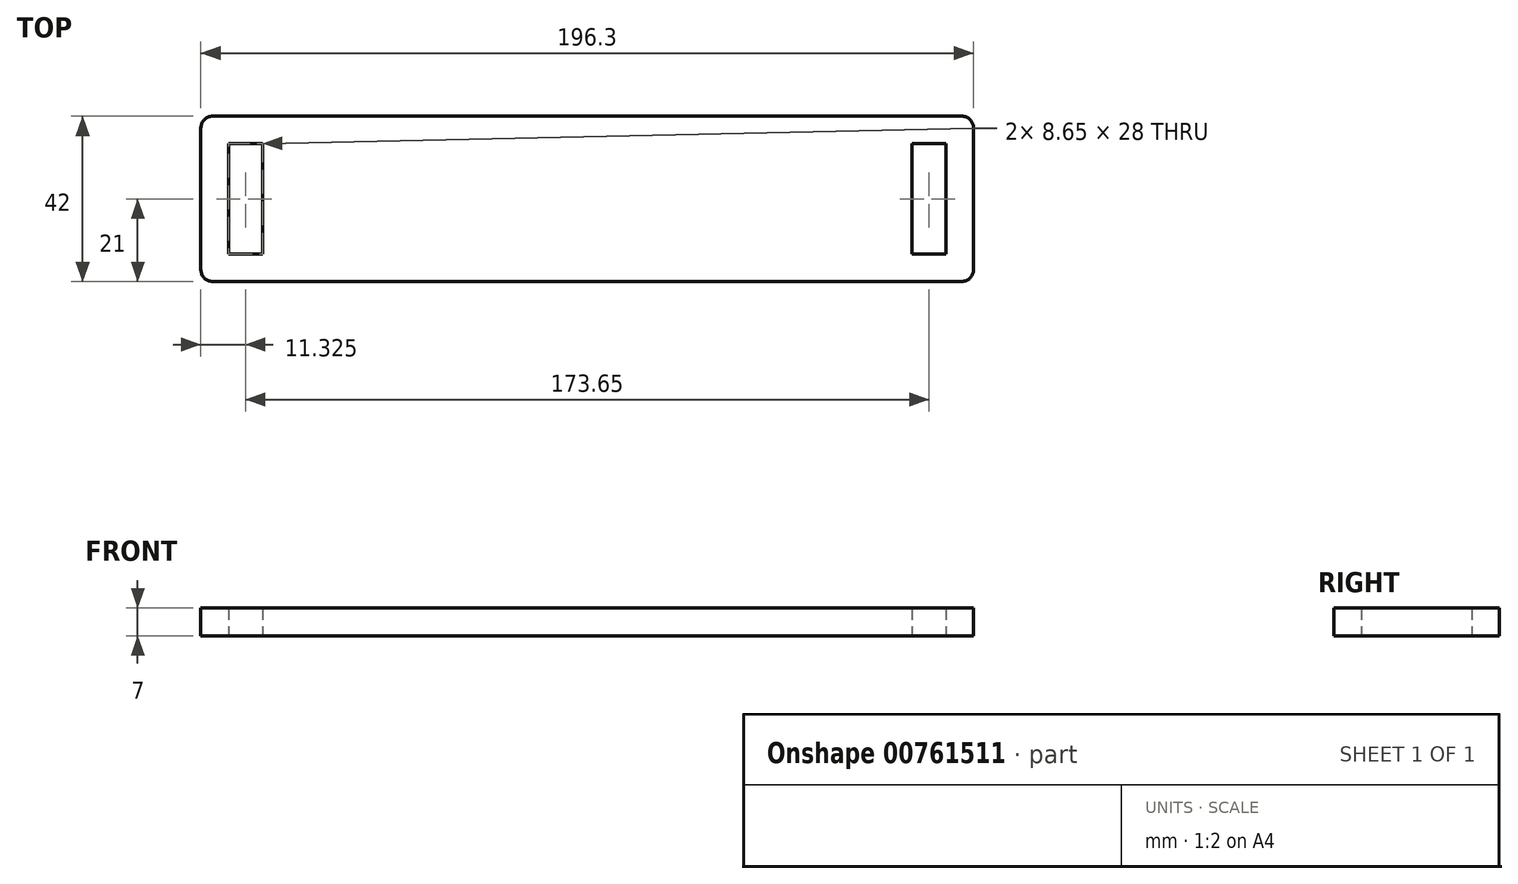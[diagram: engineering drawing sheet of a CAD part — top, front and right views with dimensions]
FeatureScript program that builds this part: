
annotation { "Feature Type Name" : "Feature", "Feature Type Description" : "" }
export const myFeature = defineFeature(function(context is Context, id is Id, definition is map)
    precondition{}
    {
        {
            var Q0;
            Q0=qCreatedBy(makeId("Top.planeOp"),FACE);
            var sketch = newSketch(context, id + "F0", { "sketchPlane" : qUnion([Q0])});
            skLineSegment(sketch, "E0.bottom", {"start": v(0, 0) * mm, "end": v(165, 0) * mm});
            skLineSegment(sketch, "E0.top", {"start": v(0, 28) * mm, "end": v(165, 28) * mm});
            skLineSegment(sketch, "E0.left", {"start": v(0, 0) * mm, "end": v(0, 28) * mm});
            skLineSegment(sketch, "E0.right", {"start": v(165, 0) * mm, "end": v(165, 28) * mm});
            skLineSegment(sketch, "E1.bottom", {"start": v(0, 28) * mm, "end": v(-8.65, 28) * mm});
            skLineSegment(sketch, "E1.top", {"start": v(0, 0) * mm, "end": v(-8.65, 0) * mm});
            skLineSegment(sketch, "E1.left", {"start": v(0, 28) * mm, "end": v(0, 0) * mm});
            skLineSegment(sketch, "E1.right", {"start": v(-8.65, 28) * mm, "end": v(-8.65, 0) * mm});
            skLineSegment(sketch, "E2.bottom", {"start": v(165, 28) * mm, "end": v(173.65, 28) * mm});
            skLineSegment(sketch, "E2.top", {"start": v(165, 0) * mm, "end": v(173.65, 0) * mm});
            skLineSegment(sketch, "E2.left", {"start": v(165, 28) * mm, "end": v(165, 0) * mm});
            skLineSegment(sketch, "E2.right", {"start": v(173.65, 28) * mm, "end": v(173.65, 0) * mm});
            skLineSegment(sketch, "E3.bottom", {"start": v(173.65, 28) * mm, "end": v(-8.65, 28) * mm});
            skLineSegment(sketch, "E3.top", {"start": v(173.65, 35) * mm, "end": v(-8.65, 35) * mm});
            skLineSegment(sketch, "E3.left", {"start": v(173.65, 28) * mm, "end": v(173.65, 35) * mm});
            skLineSegment(sketch, "E3.right", {"start": v(-8.65, 28) * mm, "end": v(-8.65, 35) * mm});
            skLineSegment(sketch, "E4.bottom", {"start": v(-8.65, 35) * mm, "end": v(-15.65, 35) * mm});
            skLineSegment(sketch, "E4.top", {"start": v(-8.65, 0) * mm, "end": v(-15.65, 0) * mm});
            skLineSegment(sketch, "E4.left", {"start": v(-8.65, 35) * mm, "end": v(-8.65, 0) * mm});
            skLineSegment(sketch, "E4.right", {"start": v(-15.65, 35) * mm, "end": v(-15.65, 0) * mm});
            skLineSegment(sketch, "E5.bottom", {"start": v(-15.65, 0) * mm, "end": v(173.65, 0) * mm});
            skLineSegment(sketch, "E5.top", {"start": v(-15.65, -7) * mm, "end": v(173.65, -7) * mm});
            skLineSegment(sketch, "E5.left", {"start": v(-15.65, 0) * mm, "end": v(-15.65, -7) * mm});
            skLineSegment(sketch, "E5.right", {"start": v(173.65, 0) * mm, "end": v(173.65, -7) * mm});
            skLineSegment(sketch, "E6.bottom", {"start": v(173.65, 35) * mm, "end": v(180.65, 35) * mm});
            skLineSegment(sketch, "E6.top", {"start": v(173.65, -7) * mm, "end": v(180.65, -7) * mm});
            skLineSegment(sketch, "E6.left", {"start": v(173.65, 35) * mm, "end": v(173.65, -7) * mm});
            skLineSegment(sketch, "E6.right", {"start": v(180.65, 35) * mm, "end": v(180.65, -7) * mm});
            skSolve(sketch);
        }
        {
            var Q0;
            Q0=makeQuery(id+"F0.imprint","IMPRINT",FACE,{"disambiguationData":[TD([[makeQuery(id+"F0.imprint","IMPRINT",EDGE,{"derivedFrom":sQuery(id+"F0.wireOp",EDGE,"E0.top")}),1.0]])]});
            var Q1;
            Q1=makeQuery(id+"F0.imprint","IMPRINT",FACE,{"disambiguationData":[TD([[makeQuery(id+"F0.imprint","IMPRINT",EDGE,{"derivedFrom":sQuery(id+"F0.wireOp",EDGE,"E1.right")}),-1.0]])]});
            var Q2;
            Q2=makeQuery(id+"F0.imprint","IMPRINT",FACE,{"disambiguationData":[TD([[makeQuery(id+"F0.imprint","IMPRINT",EDGE,{"derivedFrom":sQuery(id+"F0.wireOp",EDGE,"E0.bottom")}),-1.0]])]});
            var Q3;
            Q3=makeQuery(id+"F0.imprint","IMPRINT",FACE,{"disambiguationData":[TD([[makeQuery(id+"F0.imprint","IMPRINT",EDGE,{"derivedFrom":sQuery(id+"F0.wireOp",EDGE,"E0.bottom")}),1.0]])]});
            var Q4;
            Q4=makeQuery(id+"F0.imprint","IMPRINT",FACE,{"disambiguationData":[TD([[makeQuery(id+"F0.imprint","IMPRINT",EDGE,{"derivedFrom":sQuery(id+"F0.wireOp",EDGE,"E2.right")}),1.0]])]});
            extrude(context, id + "F1", {"entities" : qUnion([Q0, Q1, Q2, Q3, Q4]), "depth" : 7 * mm, "offsetDistance" : 25 * mm});
        }
        {
            var Q0;
            Q0=makeQuery(id+"F1.opExtrude","SWEPT_EDGE",EDGE,{"disambiguationData":[OSD([sQuery(id+"F0.wireOp",EDGE,"E6.top"),sQuery(id+"F0.wireOp",EDGE,"E6.right")])]});
            var Q1;
            Q1=makeQuery(id+"F1.opExtrude","SWEPT_EDGE",EDGE,{"disambiguationData":[OSD([sQuery(id+"F0.wireOp",EDGE,"E6.bottom"),sQuery(id+"F0.wireOp",EDGE,"E6.right")])]});
            var Q2;
            Q2=makeQuery(id+"F1.opExtrude","SWEPT_EDGE",EDGE,{"disambiguationData":[OSD([sQuery(id+"F0.wireOp",EDGE,"E5.top"),sQuery(id+"F0.wireOp",EDGE,"E5.left")])]});
            var Q3;
            Q3=makeQuery(id+"F1.opExtrude","SWEPT_EDGE",EDGE,{"disambiguationData":[OSD([sQuery(id+"F0.wireOp",EDGE,"E4.bottom"),sQuery(id+"F0.wireOp",EDGE,"E4.right")])]});
            fillet(context, id + "F2", {"entities" : qUnion([Q0, Q1, Q2, Q3]), "radius" : 3 * mm, "tangentPropagation" : true, "allowEdgeOverflow" : false});
        }
    });
